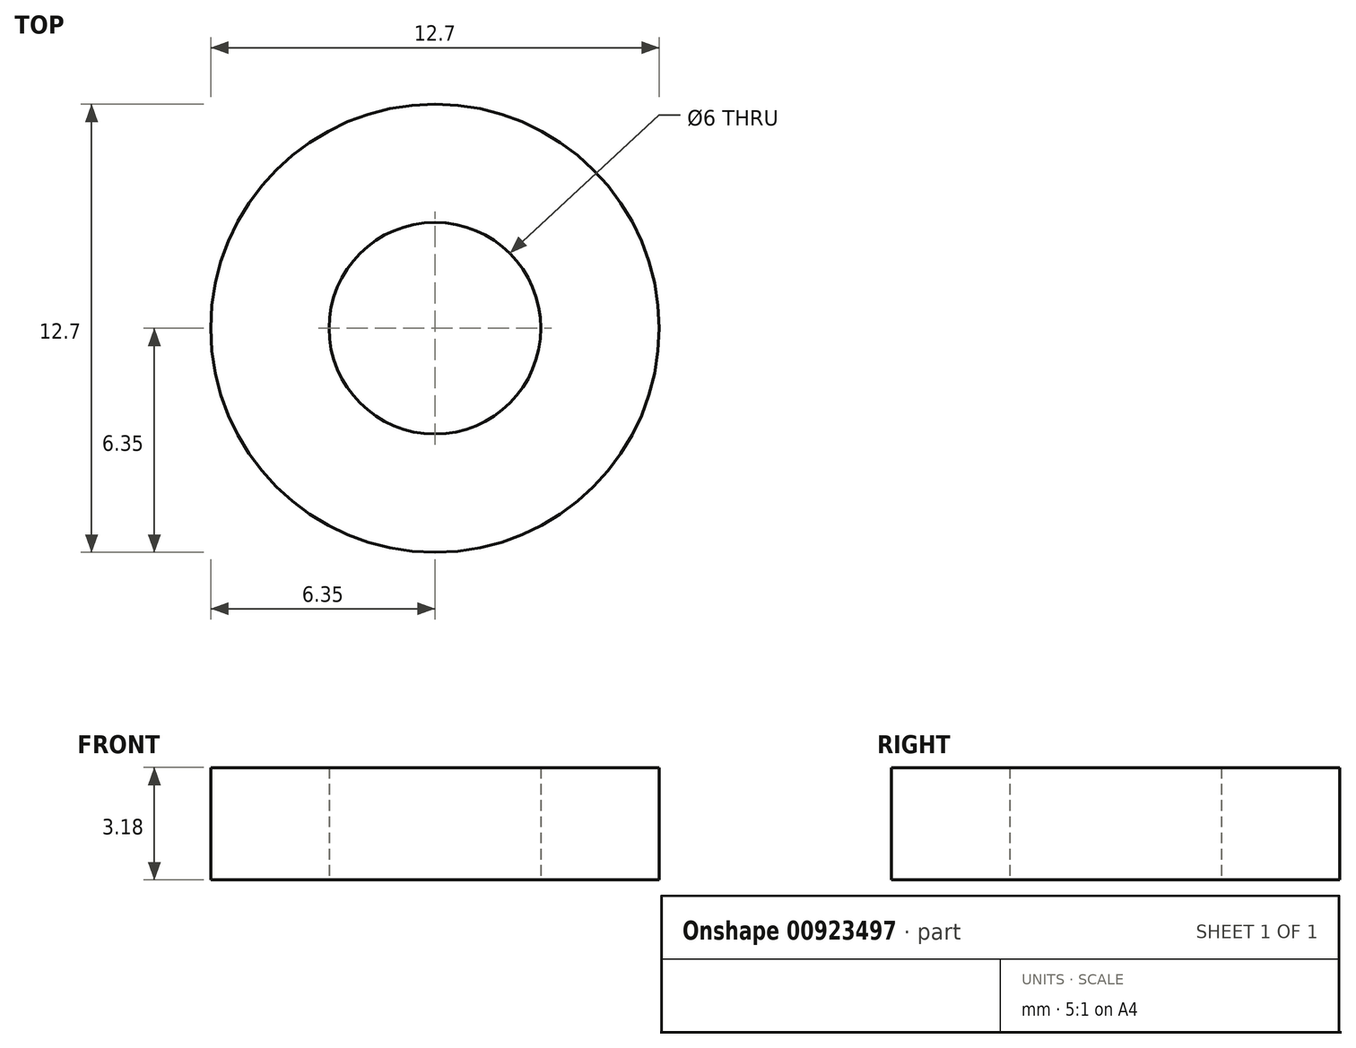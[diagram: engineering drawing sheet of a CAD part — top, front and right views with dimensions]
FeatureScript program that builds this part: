
annotation { "Feature Type Name" : "Feature", "Feature Type Description" : "" }
export const myFeature = defineFeature(function(context is Context, id is Id, definition is map)
    precondition{}
    {
        {
            var Q0;
            Q0=qCreatedBy(makeId("Top.planeOp"),FACE);
            var sketch = newSketch(context, id + "F0", { "sketchPlane" : qUnion([Q0])});
            skCircle(sketch, "E0", {"center": v(0, 0) * mm, "radius": 6.35 * mm});
            skCircle(sketch, "E1", {"center": v(0, 0) * mm, "radius": 2.25 * mm, "construction": true});
            skCircle(sketch, "E2", {"center": v(0, 0) * mm, "radius": 3 * mm});
            skSolve(sketch);
        }
        {
            var Q0;
            Q0=qSketchRegion(id+"F0",true);
            extrude(context, id + "F1", {"entities" : qUnion([Q0]), "depth" : 3.17 * mm, "offsetDistance" : 25 * mm});
        }
    });
